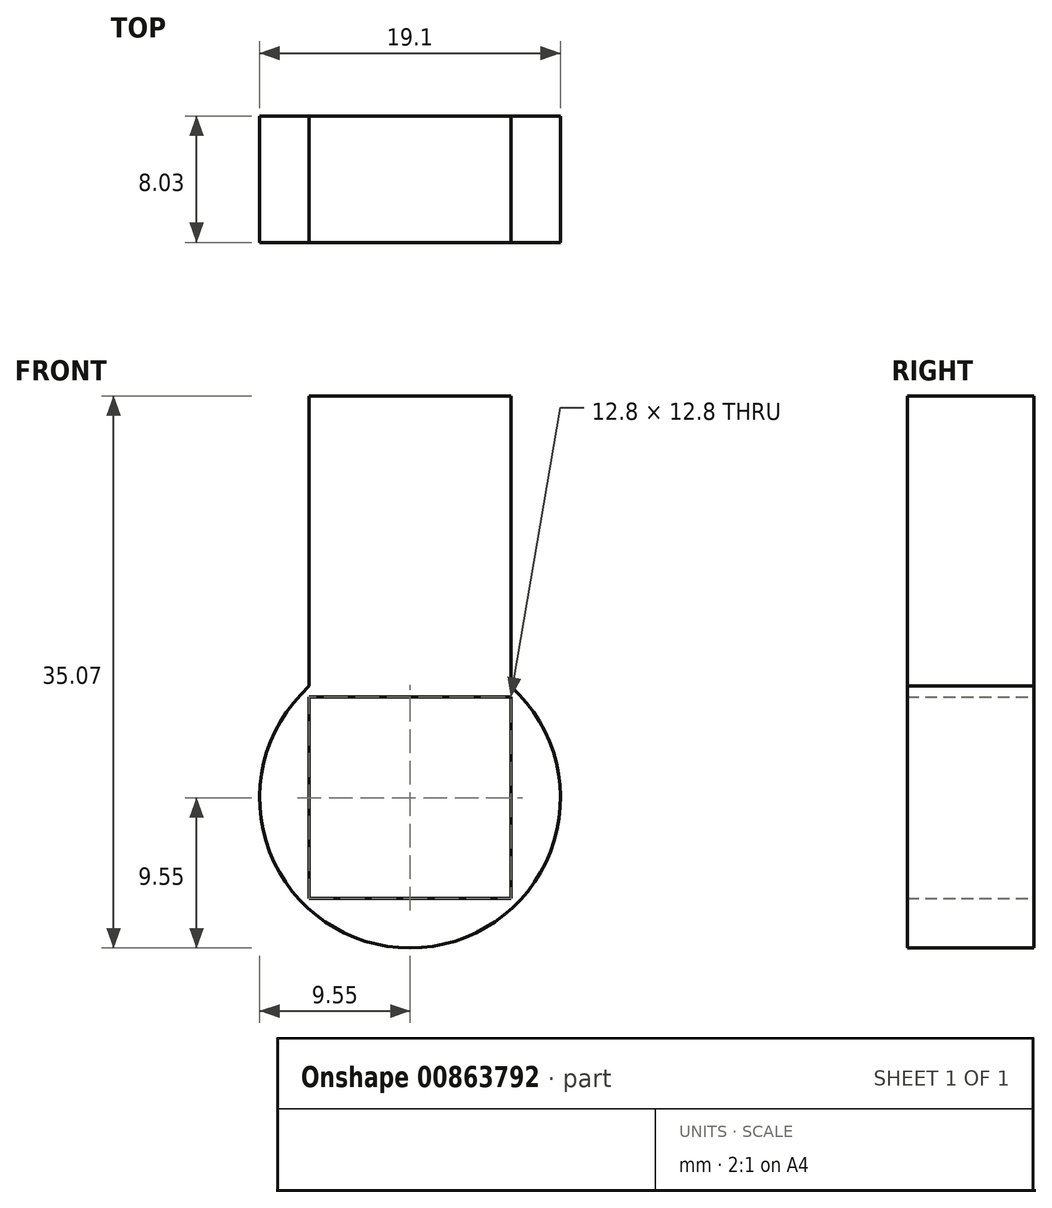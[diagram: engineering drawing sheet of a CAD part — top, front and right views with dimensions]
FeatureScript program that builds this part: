
annotation { "Feature Type Name" : "Feature", "Feature Type Description" : "" }
export const myFeature = defineFeature(function(context is Context, id is Id, definition is map)
    precondition{}
    {
        {
            var Q0;
            Q0=qCreatedBy(makeId("Front.planeOp"),FACE);
            var sketch = newSketch(context, id + "F0", { "sketchPlane" : qUnion([Q0])});
            skCircle(sketch, "E0", {"center": v(0, 0) * mm, "radius": 9.55 * mm});
            skLineSegment(sketch, "E1.rect.bottom", {"start": v(6.4, 6.4) * mm, "end": v(-6.4, 6.4) * mm});
            skLineSegment(sketch, "E1.rect.top", {"start": v(6.4, -6.4) * mm, "end": v(-6.4, -6.4) * mm});
            skLineSegment(sketch, "E1.rect.left", {"start": v(6.4, 6.4) * mm, "end": v(6.4, -6.4) * mm});
            skLineSegment(sketch, "E1.rect.right", {"start": v(-6.4, 6.4) * mm, "end": v(-6.4, -6.4) * mm});
            skSolve(sketch);
        }
        {
            var Q0;
            Q0=makeQuery(id+"F0.imprint","IMPRINT",FACE,{"disambiguationData":[TD([[makeQuery(id+"F0.imprint","IMPRINT",EDGE,{"derivedFrom":sQuery(id+"F0.wireOp",EDGE,"E0")}),1.0]])]});
            extrude(context, id + "F1", {"entities" : qUnion([Q0]), "depth" : 8.03 * mm});
        }
        {
            var Q0;
            Q0=makeQuery(id+"F1.opExtrude","SWEPT_FACE",FACE,{"disambiguationData":[OSD([sQuery(id+"F0.wireOp",EDGE,"E1.rect.bottom")])]});
            extrude(context, id + "F2", {"entities" : qUnion([Q0]), "operationType" : NewBodyOperationType.ADD, "oppositeDirection" : true, "depth" : 19.12 * mm, "offsetDistance" : 25 * mm});
        }
    });
